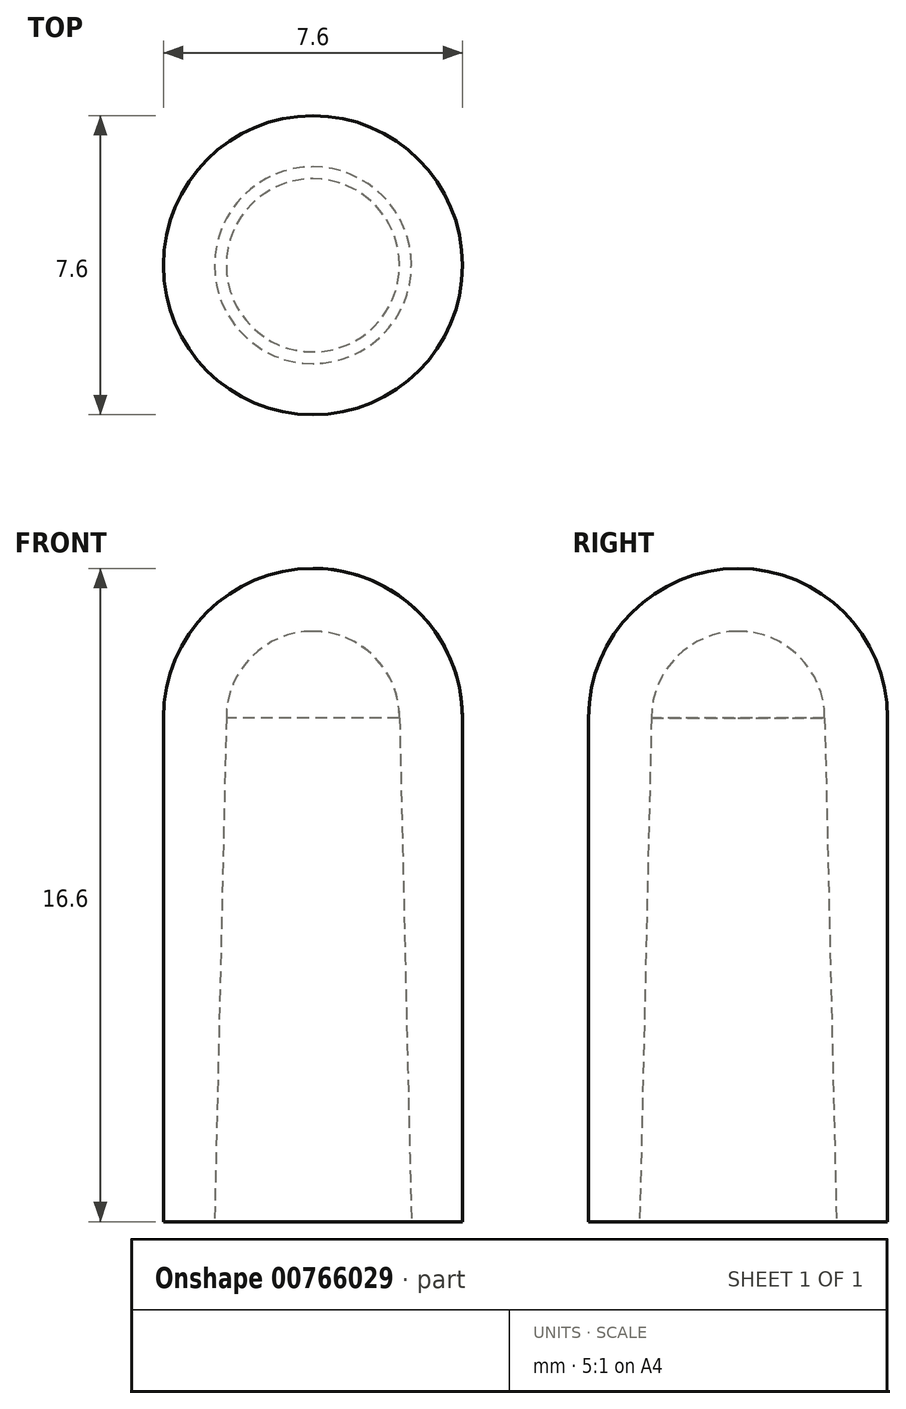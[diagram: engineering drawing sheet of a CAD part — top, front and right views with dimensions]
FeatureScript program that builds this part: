
annotation { "Feature Type Name" : "Feature", "Feature Type Description" : "" }
export const myFeature = defineFeature(function(context is Context, id is Id, definition is map)
    precondition{}
    {
        {
            var Q0;
            Q0=qCreatedBy(makeId("Front.planeOp"),FACE);
            var sketch = newSketch(context, id + "F0", { "sketchPlane" : qUnion([Q0])});
            skLineSegment(sketch, "E0", {"start": v(2.5, 0) * mm, "end": v(3.8, 0) * mm});
            skLineSegment(sketch, "E1", {"start": v(3.8, 0) * mm, "end": v(3.8, 12.8) * mm});
            skLineSegment(sketch, "E2", {"start": v(2.5, 0) * mm, "end": v(2.2, 12.8) * mm});
            skArc(sketch, "E3", {"start": v(2.2, 12.8) * mm, "mid": v(1.56, 14.36) * mm, "end": v(0, 15) * mm});
            skArc(sketch, "E4", {"start": v(3.8, 12.8) * mm, "mid": v(2.69, 15.49) * mm, "end": v(0, 16.6) * mm});
            skLineSegment(sketch, "E5", {"start": v(0, 16.6) * mm, "end": v(0, 15) * mm});
            skSolve(sketch);
        }
        {
            var Q0;
            Q0=qCreatedBy(makeId("Front.planeOp"),FACE);
            var sketch = newSketch(context, id + "F1", { "sketchPlane" : qUnion([Q0])});
            skLineSegment(sketch, "E6", {"start": v(0, 23.73) * mm, "end": v(0, 0) * mm, "construction": true});
            skSolve(sketch);
        }
        {
            var Q0;
            Q0=makeQuery(id+"F0.imprint","IMPRINT",FACE,{"disambiguationData":[TD([[makeQuery(id+"F0.imprint","IMPRINT",EDGE,{"derivedFrom":sQuery(id+"F0.wireOp",EDGE,"E0")}),1.0]])]});
            var Q1;
            Q1=sQuery(id+"F1.wireOp",EDGE,"E6");
            revolve(context, id + "F2", {"surfaceOperationType" : NewSurfaceOperationType.NEW, "entities" : qUnion([Q0]), "axis" : qUnion([Q1]), "revolveType" : RevolveType.FULL});
        }
    });
